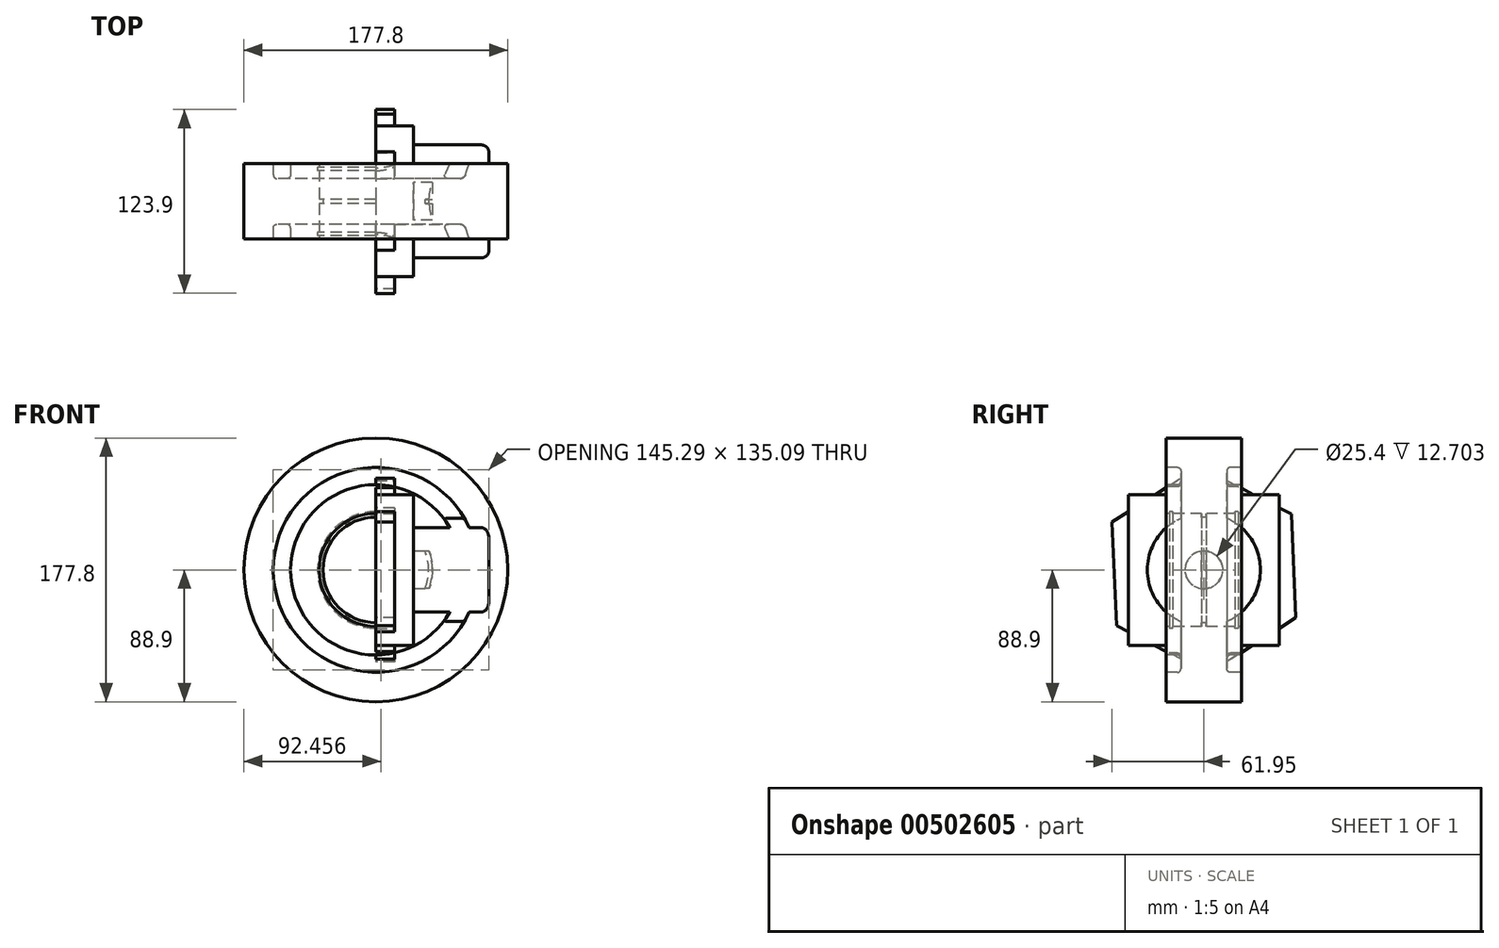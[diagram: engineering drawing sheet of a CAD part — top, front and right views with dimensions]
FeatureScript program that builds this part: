
annotation { "Feature Type Name" : "Feature", "Feature Type Description" : "" }
export const myFeature = defineFeature(function(context is Context, id is Id, definition is map)
    precondition{}
    {
        {
            var Q0;
            Q0=qCreatedBy(makeId("Right.planeOp"),FACE);
            var sketch = newSketch(context, id + "F0", { "sketchPlane" : qUnion([Q0])});
            skCircle(sketch, "E0", {"center": v(0, 0) * mm, "radius": 38.1 * mm});
            skCircle(sketch, "E1", {"center": v(0, 0) * mm, "radius": 12.7 * mm});
            skSolve(sketch);
        }
        {
            var Q0;
            Q0=makeQuery(id+"F0.imprint","IMPRINT",FACE,{"disambiguationData":[TD([[makeQuery(id+"F0.imprint","IMPRINT",EDGE,{"derivedFrom":sQuery(id+"F0.wireOp",EDGE,"E0")}),1.0]])]});
            extrude(context, id + "F1", {"entities" : qUnion([Q0]), "depth" : 76.2 * mm});
        }
        {
            var Q0;
            Q0=makeQuery(id+"F1.opExtrude","CAP_EDGE",EDGE,{"disambiguationData":[OSD([sQuery(id+"F0.wireOp",EDGE,"E0")])],"isStart":false});
            var Q1;
            Q1=makeQuery(id+"F1.opExtrude","CAP_EDGE",EDGE,{"disambiguationData":[OSD([sQuery(id+"F0.wireOp",EDGE,"E0")])],"isStart":true});
            fillet(context, id + "F2", {"entities" : qUnion([Q0, Q1]), "radius" : 5.08 * mm, "tangentPropagation" : true, "allowEdgeOverflow" : false});
        }
        {
            var Q0;
            Q0=sQuery(id+"F0.wireOp",EDGE,"E1");
            extrude(context, id + "F3", {"bodyType" : ToolBodyType.SURFACE, "surfaceEntities" : qUnion([Q0]), "depth" : 114.3 * mm});
        }
        {
            var Q0;
            Q0=qCreatedBy(makeId("Right.planeOp"),FACE);
            var sketch = newSketch(context, id + "F4", { "sketchPlane" : qUnion([Q0])});
            skLineSegment(sketch, "E2.bottom", {"start": v(50.8, -50.8) * mm, "end": v(-50.8, -50.8) * mm});
            skLineSegment(sketch, "E2.top", {"start": v(50.8, 50.8) * mm, "end": v(-50.8, 50.8) * mm});
            skLineSegment(sketch, "E2.left", {"start": v(50.8, -50.8) * mm, "end": v(50.8, 50.8) * mm});
            skLineSegment(sketch, "E2.right", {"start": v(-50.8, -50.8) * mm, "end": v(-50.8, 50.8) * mm});
            skPoint(sketch, "E2.middle", {"position": v(0, 0) * mm});
            skSolve(sketch);
        }
        {
            var Q0;
            Q0=makeQuery(id+"F4.imprint","IMPRINT",FACE,{"disambiguationData":[TD([[makeQuery(id+"F4.imprint","IMPRINT",EDGE,{"derivedFrom":sQuery(id+"F4.wireOp",EDGE,"E2.bottom")}),-1.0]])]});
            extrude(context, id + "F5", {"entities" : qUnion([Q0]), "operationType" : NewBodyOperationType.ADD, "depth" : 25.4 * mm});
        }
        {
            var Q0;
            Q0=qCreatedBy(makeId("Right.planeOp"),FACE);
            var sketch = newSketch(context, id + "F6", { "sketchPlane" : qUnion([Q0])});
            skCircle(sketch, "E3.cCircle", {"center": v(0, 0) * mm, "radius": 69.85 * mm, "construction": true});
            skLineSegment(sketch, "E3.0", {"start": v(61.95, -32.26) * mm, "end": v(3.03, -69.78) * mm});
            skLineSegment(sketch, "E3.1", {"start": v(3.03, -69.78) * mm, "end": v(-58.92, -37.52) * mm});
            skLineSegment(sketch, "E3.2", {"start": v(-58.92, -37.52) * mm, "end": v(-61.95, 32.26) * mm});
            skLineSegment(sketch, "E3.3", {"start": v(-61.95, 32.26) * mm, "end": v(-3.03, 69.78) * mm});
            skLineSegment(sketch, "E3.4", {"start": v(-3.03, 69.78) * mm, "end": v(58.92, 37.52) * mm});
            skLineSegment(sketch, "E3.5", {"start": v(58.92, 37.52) * mm, "end": v(61.95, -32.26) * mm});
            skSolve(sketch);
        }
        {
            var Q0;
            Q0=makeQuery(id+"F6.imprint","IMPRINT",FACE,{"disambiguationData":[TD([[makeQuery(id+"F6.imprint","IMPRINT",EDGE,{"derivedFrom":sQuery(id+"F6.wireOp",EDGE,"E3.0")}),-1.0]])]});
            extrude(context, id + "F7", {"entities" : qUnion([Q0]), "operationType" : NewBodyOperationType.ADD, "depth" : 12.7 * mm});
        }
        {
            var Q0;
            Q0=qCreatedBy(makeId("Right.planeOp"),FACE);
            var sketch = newSketch(context, id + "F8", { "sketchPlane" : qUnion([Q0])});
            skLineSegment(sketch, "E4.bottom", {"start": v(0, 0) * mm, "end": v(25.4, 0) * mm, "construction": true});
            skLineSegment(sketch, "E4.top", {"start": v(0, 88.9) * mm, "end": v(25.4, 88.9) * mm});
            skLineSegment(sketch, "E4.left", {"start": v(0, 0) * mm, "end": v(0, 88.9) * mm, "construction": true});
            skLineSegment(sketch, "E5", {"start": v(25.4, 38.1) * mm, "end": v(23.11, 38.1) * mm});
            skLineSegment(sketch, "E6", {"start": v(23.11, 38.1) * mm, "end": v(23.11, 39.38) * mm});
            skLineSegment(sketch, "E7", {"start": v(20.83, 39.38) * mm, "end": v(20.83, 38.1) * mm});
            skLineSegment(sketch, "E8", {"start": v(20.83, 38.1) * mm, "end": v(1.52, 38.1) * mm});
            skLineSegment(sketch, "E9", {"start": v(23.11, 39.38) * mm, "end": v(20.83, 39.38) * mm});
            skLineSegment(sketch, "E10", {"start": v(1.52, 38.1) * mm, "end": v(1.52, 35.56) * mm});
            skLineSegment(sketch, "E11", {"start": v(1.52, 35.56) * mm, "end": v(0, 35.56) * mm});
            skLineSegment(sketch, "E12", {"start": v(25.4, 57.4) * mm, "end": v(17.95, 57.4) * mm});
            skLineSegment(sketch, "E13", {"start": v(15.4, 59.94) * mm, "end": v(15.4, 66.55) * mm});
            skLineSegment(sketch, "E14", {"start": v(17.95, 69.09) * mm, "end": v(25.4, 69.09) * mm});
            skLineSegment(sketch, "E15.trimOffspring", {"start": v(25.4, 69.09) * mm, "end": v(25.4, 88.9) * mm});
            skPoint(sketch, "E16.visualSharp", {"position": v(15.4, 69.09) * mm});
            skArc(sketch, "E16.filletArc", {"start": v(17.95, 69.09) * mm, "mid": v(16.15, 68.34) * mm, "end": v(15.4, 66.55) * mm});
            skPoint(sketch, "E17.visualSharp", {"position": v(15.4, 57.4) * mm});
            skArc(sketch, "E17.filletArc", {"start": v(15.4, 59.94) * mm, "mid": v(16.15, 58.15) * mm, "end": v(17.95, 57.4) * mm});
            skLineSegment(sketch, "E18.MirrorCS", {"start": v(0, 88.9) * mm, "end": v(-25.4, 88.9) * mm});
            skLineSegment(sketch, "E19.MirrorCS", {"start": v(-25.4, 69.09) * mm, "end": v(-25.4, 88.9) * mm});
            skLineSegment(sketch, "E20.MirrorCS", {"start": v(-17.95, 69.09) * mm, "end": v(-25.4, 69.09) * mm});
            skArc(sketch, "E21.MirrorCS", {"start": v(-17.95, 69.09) * mm, "mid": v(-16.15, 68.34) * mm, "end": v(-15.4, 66.55) * mm});
            skLineSegment(sketch, "E22.MirrorCS", {"start": v(-15.4, 59.94) * mm, "end": v(-15.4, 66.55) * mm});
            skArc(sketch, "E23.MirrorCS", {"start": v(-15.4, 59.94) * mm, "mid": v(-16.15, 58.15) * mm, "end": v(-17.95, 57.4) * mm});
            skLineSegment(sketch, "E24.MirrorCS", {"start": v(-25.4, 57.4) * mm, "end": v(-17.95, 57.4) * mm});
            skLineSegment(sketch, "E25", {"start": v(25.4, 57.4) * mm, "end": v(25.4, 38.1) * mm});
            skLineSegment(sketch, "E26.MirrorCS", {"start": v(-25.4, 57.4) * mm, "end": v(-25.4, 38.1) * mm});
            skLineSegment(sketch, "E27.MirrorCS", {"start": v(-25.4, 38.1) * mm, "end": v(-23.11, 38.1) * mm});
            skLineSegment(sketch, "E28.MirrorCS", {"start": v(-23.11, 38.1) * mm, "end": v(-23.11, 39.38) * mm});
            skLineSegment(sketch, "E29.MirrorCS", {"start": v(-23.11, 39.38) * mm, "end": v(-20.83, 39.38) * mm});
            skLineSegment(sketch, "E30.MirrorCS", {"start": v(-20.83, 39.38) * mm, "end": v(-20.83, 38.1) * mm});
            skLineSegment(sketch, "E31.MirrorCS", {"start": v(-20.83, 38.1) * mm, "end": v(-1.52, 38.1) * mm});
            skLineSegment(sketch, "E32.MirrorCS", {"start": v(-1.52, 38.1) * mm, "end": v(-1.52, 35.56) * mm});
            skLineSegment(sketch, "E33.MirrorCS", {"start": v(-1.52, 35.56) * mm, "end": v(0, 35.56) * mm});
            skPoint(sketch, "E34.MirrorCS.end.orphan", {"position": v(-25.4, 38.1) * mm});
            skPoint(sketch, "E34.MirrorCS.start.orphan", {"position": v(-25.4, 0) * mm});
            skSolve(sketch);
        }
        {
            var Q0;
            Q0=makeQuery(id+"F8.imprint","IMPRINT",FACE,{"disambiguationData":[TD([[makeQuery(id+"F8.imprint","IMPRINT",EDGE,{"derivedFrom":sQuery(id+"F8.wireOp",EDGE,"E4.top")}),-1.0]])]});
            var Q1;
            Q1=sQuery(id+"F8.wireOp",EDGE,"E4.bottom");
            revolve(context, id + "F9", {"operationType" : NewBodyOperationType.ADD, "entities" : qUnion([Q0]), "axis" : qUnion([Q1]), "revolveType" : RevolveType.FULL});
        }
    });
